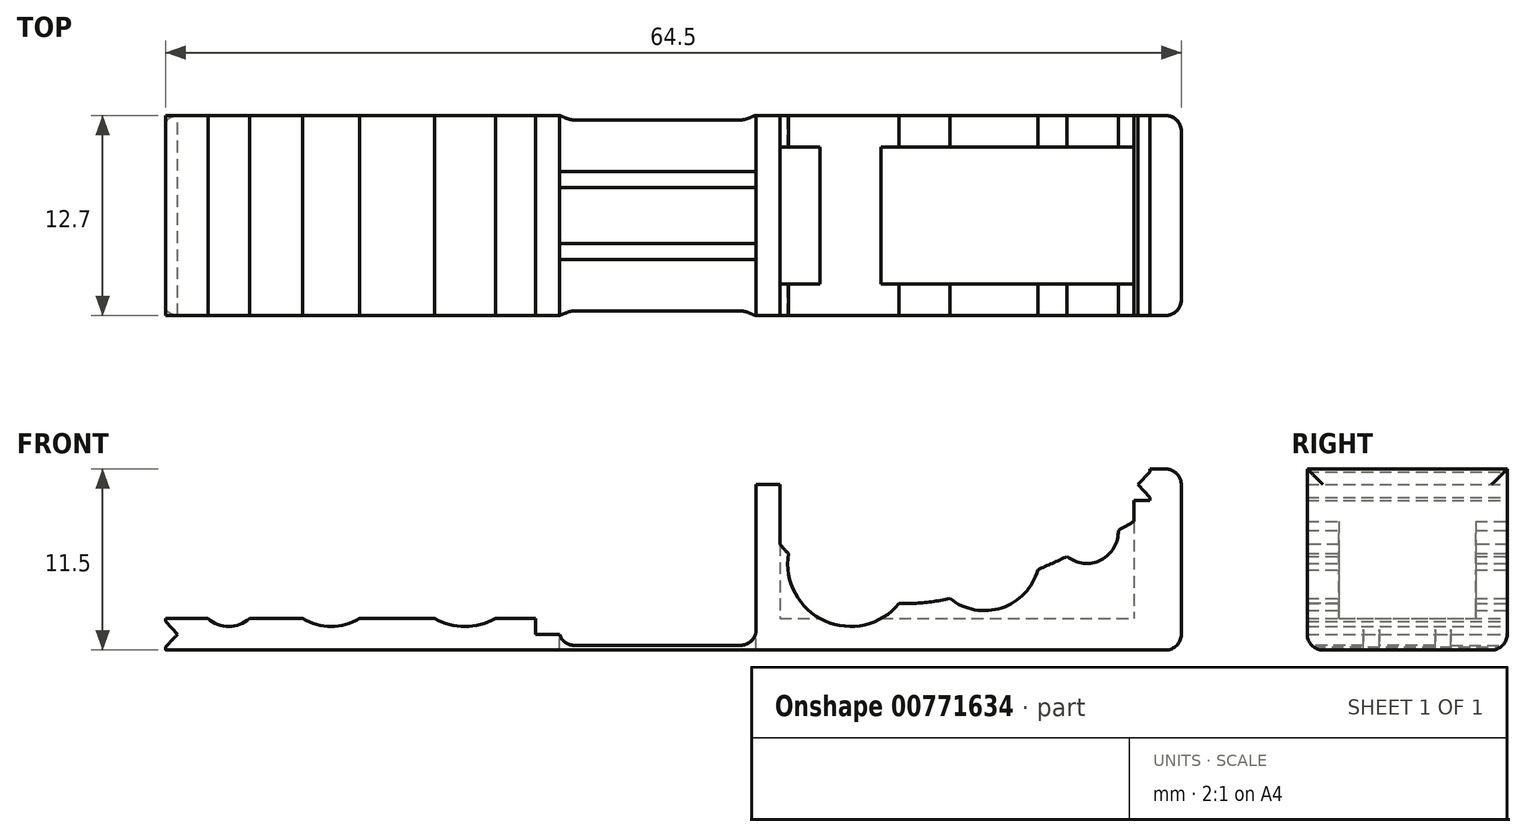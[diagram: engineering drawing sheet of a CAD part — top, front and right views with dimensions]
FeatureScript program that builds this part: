
annotation { "Feature Type Name" : "Feature", "Feature Type Description" : "" }
export const myFeature = defineFeature(function(context is Context, id is Id, definition is map)
    precondition{}
    {
        {
            var Q0;
            Q0=qCreatedBy(makeId("Front.planeOp"),FACE);
            var sketch = newSketch(context, id + "F0", { "sketchPlane" : qUnion([Q0])});
            skCircle(sketch, "E0", {"center": v(-12.25, 5.5) * mm, "radius": 4 * mm});
            skCircle(sketch, "E1", {"center": v(-20.75, 5) * mm, "radius": 3.5 * mm});
            skCircle(sketch, "E2", {"center": v(-27.25, 3.5) * mm, "radius": 2 * mm});
            skPoint(sketch, "E3", {"position": v(-20.75, 1.5) * mm});
            skPoint(sketch, "E4", {"position": v(-27.25, 1.5) * mm});
            skPoint(sketch, "E5", {"position": v(-12.25, 1.5) * mm});
            skLineSegment(sketch, "E6", {"start": v(-25.25, 1.5) * mm, "end": v(-24.25, 1.5) * mm});
            skLineSegment(sketch, "E7", {"start": v(-17.25, 1.5) * mm, "end": v(-16.25, 1.5) * mm});
            skPoint(sketch, "E8", {"position": v(-25.25, 3.5) * mm});
            skPoint(sketch, "E9", {"position": v(-24.25, 5) * mm});
            skPoint(sketch, "E10", {"position": v(-29.25, 3.5) * mm});
            skPoint(sketch, "E11", {"position": v(-17.25, 5) * mm});
            skPoint(sketch, "E12", {"position": v(-16.25, 5.5) * mm});
            skPoint(sketch, "E13", {"position": v(-8.25, 5.5) * mm});
            skPoint(sketch, "E14", {"position": v(0, 5.5) * mm});
            skPoint(sketch, "E15", {"position": v(12.25, 1.5) * mm});
            skCircle(sketch, "E16.1.0", {"center": v(12.25, 5.5) * mm, "radius": 4 * mm});
            skCircle(sketch, "E16.1.1", {"center": v(20.75, 6) * mm, "radius": 3.5 * mm});
            skCircle(sketch, "E16.1.2", {"center": v(27.25, 7.5) * mm, "radius": 2 * mm});
            skSolve(sketch);
        }
        {
            var Q0;
            Q0=qCreatedBy(makeId("Front.planeOp"),FACE);
            var sketch = newSketch(context, id + "F1", { "sketchPlane" : qUnion([Q0])});
            skCircle(sketch, "E17.0", {"center": v(-27.25, 3.5) * mm, "radius": 2 * mm});
            skCircle(sketch, "E18.0", {"center": v(-20.75, 5) * mm, "radius": 3.5 * mm});
            skCircle(sketch, "E19.0", {"center": v(-12.25, 5.5) * mm, "radius": 4 * mm});
            skLineSegment(sketch, "E20.bottom", {"start": v(-31.25, 2) * mm, "end": v(-6.25, 2) * mm});
            skLineSegment(sketch, "E20.top", {"start": v(-31.25, 0) * mm, "end": v(-6.25, 0) * mm});
            skLineSegment(sketch, "E20.left", {"start": v(-31.25, 2) * mm, "end": v(-31.25, 0) * mm});
            skLineSegment(sketch, "E20.right", {"start": v(-6.25, 2) * mm, "end": v(-6.25, 0) * mm});
            skLineSegment(sketch, "E21.bottom", {"start": v(6.25, 0) * mm, "end": v(31.25, 0) * mm});
            skLineSegment(sketch, "E21.left", {"start": v(6.25, 0) * mm, "end": v(6.25, 8.72) * mm});
            skLineSegment(sketch, "E21.right", {"start": v(31.25, 0) * mm, "end": v(31.25, 8.72) * mm});
            skLineSegment(sketch, "E22.bottom", {"start": v(-6.25, 0.3) * mm, "end": v(6.25, 0.3) * mm});
            skLineSegment(sketch, "E22.top", {"start": v(-6.25, 0) * mm, "end": v(6.25, 0) * mm});
            skLineSegment(sketch, "E22.left", {"start": v(-6.25, 0.3) * mm, "end": v(-6.25, 0) * mm});
            skLineSegment(sketch, "E22.right", {"start": v(6.25, 0.3) * mm, "end": v(6.25, 0) * mm});
            skPoint(sketch, "E23", {"position": v(0, 0) * mm});
            skFitSpline(sketch, "E24", {"points": [v(6.25, 8.72) * mm, v(31.25, 8.72) * mm], "startDerivative": vector(15.22, -23.1) * mm, "endDerivative": vector(40.47, 23.1) * mm});
            skCircle(sketch, "E25.0", {"center": v(12.25, 5.5) * mm, "radius": 4 * mm});
            skCircle(sketch, "E26.0", {"center": v(20.75, 6) * mm, "radius": 3.5 * mm});
            skCircle(sketch, "E27.0", {"center": v(27.25, 7.5) * mm, "radius": 2 * mm});
            skSolve(sketch);
        }
        {
            var Q0;
            Q0=makeQuery(id+"F1.imprint","IMPRINT",FACE,{"disambiguationData":[TD([[makeQuery(id+"F1.imprint","IMPRINT",EDGE,{"derivedFrom":sQuery(id+"F1.wireOp",EDGE,"E20.top")}),1.0]])]});
            var Q1;
            Q1=makeQuery(id+"F1.imprint","IMPRINT",FACE,{"disambiguationData":[TD([[makeQuery(id+"F1.imprint","IMPRINT",EDGE,{"derivedFrom":sQuery(id+"F1.wireOp",EDGE,"E22.bottom")}),-1.0]])]});
            var Q2;
            Q2=makeQuery(id+"F1.imprint","IMPRINT",FACE,{"disambiguationData":[TD([[makeQuery(id+"F1.imprint","IMPRINT",EDGE,{"derivedFrom":sQuery(id+"F1.wireOp",EDGE,"E21.bottom")}),1.0]])]});
            extrude(context, id + "F2", {"entities" : qUnion([Q0, Q1, Q2]), "depth" : 12.7 * mm, "offsetDistance" : 25 * mm});
        }
        {
            var Q0;
            Q0=makeQuery(id+"F2.opExtrude","SWEPT_FACE",FACE,{"disambiguationData":[OSD([sQuery(id+"F1.wireOp",EDGE,"E21.right")])]});
            var sketch = newSketch(context, id + "F3", { "sketchPlane" : qUnion([Q0])});
            skLineSegment(sketch, "E28.bottom", {"start": v(-10.7, 8.72) * mm, "end": v(-2, 8.72) * mm});
            skLineSegment(sketch, "E28.top", {"start": v(-10.7, 2) * mm, "end": v(-2, 2) * mm});
            skLineSegment(sketch, "E28.left", {"start": v(-10.7, 8.72) * mm, "end": v(-10.7, 2) * mm});
            skLineSegment(sketch, "E28.right", {"start": v(-2, 8.72) * mm, "end": v(-2, 2) * mm});
            skPoint(sketch, "E29", {"position": v(-6.35, 8.72) * mm});
            skSolve(sketch);
        }
        {
            var Q0;
            Q0=qCreatedBy(makeId("Front.planeOp"),FACE);
            var sketch = newSketch(context, id + "F4", { "sketchPlane" : qUnion([Q0])});
            skLineSegment(sketch, "E30.0", {"start": v(-31.25, 2) * mm, "end": v(-31.25, 0) * mm});
            skLineSegment(sketch, "E31", {"start": v(-30.5, 1) * mm, "end": v(-31.25, 0.2) * mm});
            skLineSegment(sketch, "E32", {"start": v(31.25, 0) * mm, "end": v(33.25, 0) * mm});
            skLineSegment(sketch, "E33", {"start": v(33.25, 0) * mm, "end": v(33.25, 11.5) * mm});
            skLineSegment(sketch, "E34", {"start": v(33.25, 11.5) * mm, "end": v(31.25, 11.5) * mm});
            skLineSegment(sketch, "E35", {"start": v(31.25, 11.5) * mm, "end": v(31.25, 11.3) * mm});
            skLineSegment(sketch, "E36", {"start": v(31.25, 11.3) * mm, "end": v(30.5, 10.5) * mm});
            skLineSegment(sketch, "E37", {"start": v(30.5, 10.5) * mm, "end": v(31.25, 9.7) * mm});
            skLineSegment(sketch, "E38", {"start": v(31.25, 9.7) * mm, "end": v(31.25, 9.5) * mm});
            skLineSegment(sketch, "E39", {"start": v(31.25, 9.5) * mm, "end": v(30.25, 9.5) * mm});
            skLineSegment(sketch, "E40", {"start": v(30.25, 9.5) * mm, "end": v(30.25, 0) * mm});
            skPoint(sketch, "E41.0", {"position": v(-6.25, 2) * mm});
            skLineSegment(sketch, "E42.bottom", {"start": v(-6.25, 2) * mm, "end": v(-7.75, 2) * mm});
            skLineSegment(sketch, "E42.top", {"start": v(-6.25, 1) * mm, "end": v(-7.75, 1) * mm});
            skLineSegment(sketch, "E42.left", {"start": v(-6.25, 2) * mm, "end": v(-6.25, 1) * mm});
            skLineSegment(sketch, "E42.right", {"start": v(-7.75, 2) * mm, "end": v(-7.75, 1) * mm});
            skLineSegment(sketch, "E43", {"start": v(6.25, 0) * mm, "end": v(6.25, 11.5) * mm});
            skLineSegment(sketch, "E44", {"start": v(6.25, 11.5) * mm, "end": v(7.75, 11.5) * mm});
            skLineSegment(sketch, "E45", {"start": v(7.75, 11.5) * mm, "end": v(7.75, 0) * mm});
            skLineSegment(sketch, "E46", {"start": v(7.75, 10.5) * mm, "end": v(6.25, 10.5) * mm});
            skLineSegment(sketch, "E47", {"start": v(-31.25, 0.2) * mm, "end": v(-31.25, 0) * mm});
            skLineSegment(sketch, "E48", {"start": v(-30.5, 1) * mm, "end": v(-31.25, 1.8) * mm});
            skLineSegment(sketch, "E49", {"start": v(-30.5, 1) * mm, "end": v(-31.25, 1) * mm});
            skLineSegment(sketch, "E50", {"start": v(31.25, 11.3) * mm, "end": v(31.25, 9.7) * mm});
            skLineSegment(sketch, "E51", {"start": v(30.5, 10.5) * mm, "end": v(31.25, 10.5) * mm});
            skLineSegment(sketch, "E52", {"start": v(6.25, 0) * mm, "end": v(7.75, 0) * mm});
            skLineSegment(sketch, "E53", {"start": v(31.25, 0) * mm, "end": v(30.25, 0) * mm});
            skSolve(sketch);
        }
        {
            var Q0;
            Q0=makeQuery(id+"F3.imprint","IMPRINT",FACE,{"disambiguationData":[TD([[makeQuery(id+"F3.imprint","IMPRINT",EDGE,{"derivedFrom":sQuery(id+"F3.wireOp",EDGE,"E28.bottom")}),-1.0]])]});
            var Q1;
            Q1=sQuery(id+"F4.wireOp",VERTEX,"E44.end");
            var Q2;
            Q2=sQuery(id+"F4.wireOp",VERTEX,"E39.end");
            extrude(context, id + "F5", {"entities" : qUnion([Q0]), "operationType" : NewBodyOperationType.REMOVE, "endBound" : BoundingType.UP_TO_VERTEX, "oppositeDirection" : true, "depth" : 25 * mm, "endBoundEntityVertex" : qUnion([Q1]), "offsetDistance" : 25 * mm, "hasSecondDirection" : true, "secondDirectionBound" : SecondDirectionBoundingType.UP_TO_VERTEX, "secondDirectionOppositeDirection" : true, "secondDirectionDepth" : 1 * mm, "secondDirectionBoundEntityVertex" : qUnion([Q2])});
        }
        {
            var Q0;
            Q0=makeQuery(id+"F4.imprint","IMPRINT",FACE,{"disambiguationData":[TD([[makeQuery(id+"F4.imprint","IMPRINT",EDGE,{"derivedFrom":sQuery(id+"F4.wireOp",EDGE,"E42.bottom")}),1.0]])]});
            var Q1;
            {var subQ0=sQuery(id+"F4.wireOp",EDGE,"E48");Q1=makeQuery(id+"F4.imprint","IMPRINT",FACE,{"disambiguationData":[TD([[makeQuery(id+"F4.imprint","IMPRINT",EDGE,{"derivedFrom":subQ0}),1.0]])]});}
            var Q2;
            {var subQ0=sQuery(id+"F4.wireOp",EDGE,"E31");Q2=makeQuery(id+"F4.imprint","IMPRINT",FACE,{"disambiguationData":[TD([[makeQuery(id+"F4.imprint","IMPRINT",EDGE,{"derivedFrom":subQ0}),-1.0]])]});}
            var Q3;
            Q3=makeQuery(id+"F2.opExtrude","CAP_FACE",FACE,{"disambiguationData":[OSD([sQuery(id+"F1.wireOp",EDGE,"E17.0"),sQuery(id+"F1.wireOp",EDGE,"E18.0"),sQuery(id+"F1.wireOp",EDGE,"E19.0"),sQuery(id+"F1.wireOp",EDGE,"39558c70-f25f-4615-a4fc-9f10651319aa.0"),sQuery(id+"F1.wireOp",EDGE,"80cb3f8d-76fc-4d8c-9657-01cc7cf24295.0"),sQuery(id+"F1.wireOp",EDGE,"e33433a3-29e9-4e5c-a5f5-65428797577c.0"),sQuery(id+"F1.wireOp",EDGE,"f559ebbb-155e-4eeb-81d7-9a44377361a2.0"),sQuery(id+"F1.wireOp",EDGE,"83c2658b-0a7b-448c-8bf9-07c5c6f78f0d.0"),sQuery(id+"F1.wireOp",EDGE,"bfc84c2d-0466-46b3-b6ee-57e5656d9882.0"),sQuery(id+"F1.wireOp",EDGE,"843dab0d-1d24-4ee7-8fdb-ab5b204e5594.0"),sQuery(id+"F1.wireOp",EDGE,"b1db5fe8-4577-4f43-9009-2c0ead2f0b42.0"),sQuery(id+"F1.wireOp",EDGE,"7c9d848a-de27-417e-884b-11b5ffe38909.0"),sQuery(id+"F1.wireOp",EDGE,"E20.bottom"),sQuery(id+"F1.wireOp",EDGE,"E20.top"),sQuery(id+"F1.wireOp",EDGE,"E20.left"),sQuery(id+"F1.wireOp",EDGE,"E20.right"),sQuery(id+"F1.wireOp",EDGE,"E21.bottom"),sQuery(id+"F1.wireOp",EDGE,"E21.left"),sQuery(id+"F1.wireOp",EDGE,"E21.right"),sQuery(id+"F1.wireOp",EDGE,"E22.bottom"),sQuery(id+"F1.wireOp",EDGE,"E22.top"),sQuery(id+"F1.wireOp",EDGE,"E24")])],"isStart":false});
            extrude(context, id + "F6", {"entities" : qUnion([Q0, Q1, Q2]), "operationType" : NewBodyOperationType.REMOVE, "endBound" : BoundingType.UP_TO_SURFACE, "depth" : 25 * mm, "endBoundEntityFace" : qUnion([Q3]), "offsetDistance" : 25 * mm});
        }
        {
            var Q0;
            Q0=makeQuery(id+"F4.imprint","IMPRINT",FACE,{"disambiguationData":[TD([[makeQuery(id+"F4.imprint","IMPRINT",EDGE,{"derivedFrom":sQuery(id+"F4.wireOp",EDGE,"E32")}),1.0]])]});
            var Q1;
            {var subQ2=sQuery(id+"F4.wireOp",EDGE,"E46");Q1=makeQuery(id+"F4.imprint","IMPRINT",FACE,{"disambiguationData":[TD([[makeQuery(id+"F4.imprint","IMPRINT",EDGE,{"derivedFrom":subQ2}),1.0]])]});}
            var Q2;
            {var subQ0=sQuery(id+"F4.wireOp",EDGE,"E37");Q2=makeQuery(id+"F4.imprint","IMPRINT",FACE,{"disambiguationData":[TD([[makeQuery(id+"F4.imprint","IMPRINT",EDGE,{"derivedFrom":subQ0}),1.0]])]});}
            var Q3;
            {var subQ0=sQuery(id+"F4.wireOp",EDGE,"E36");Q3=makeQuery(id+"F4.imprint","IMPRINT",FACE,{"disambiguationData":[TD([[makeQuery(id+"F4.imprint","IMPRINT",EDGE,{"derivedFrom":subQ0}),1.0]])]});}
            var Q4;
            Q4=makeQuery(id+"F2.opExtrude","CAP_FACE",FACE,{"disambiguationData":[OSD([sQuery(id+"F1.wireOp",EDGE,"E17.0"),sQuery(id+"F1.wireOp",EDGE,"E18.0"),sQuery(id+"F1.wireOp",EDGE,"E19.0"),sQuery(id+"F1.wireOp",EDGE,"39558c70-f25f-4615-a4fc-9f10651319aa.0"),sQuery(id+"F1.wireOp",EDGE,"80cb3f8d-76fc-4d8c-9657-01cc7cf24295.0"),sQuery(id+"F1.wireOp",EDGE,"e33433a3-29e9-4e5c-a5f5-65428797577c.0"),sQuery(id+"F1.wireOp",EDGE,"f559ebbb-155e-4eeb-81d7-9a44377361a2.0"),sQuery(id+"F1.wireOp",EDGE,"83c2658b-0a7b-448c-8bf9-07c5c6f78f0d.0"),sQuery(id+"F1.wireOp",EDGE,"bfc84c2d-0466-46b3-b6ee-57e5656d9882.0"),sQuery(id+"F1.wireOp",EDGE,"843dab0d-1d24-4ee7-8fdb-ab5b204e5594.0"),sQuery(id+"F1.wireOp",EDGE,"b1db5fe8-4577-4f43-9009-2c0ead2f0b42.0"),sQuery(id+"F1.wireOp",EDGE,"7c9d848a-de27-417e-884b-11b5ffe38909.0"),sQuery(id+"F1.wireOp",EDGE,"E20.bottom"),sQuery(id+"F1.wireOp",EDGE,"E20.top"),sQuery(id+"F1.wireOp",EDGE,"E20.left"),sQuery(id+"F1.wireOp",EDGE,"E20.right"),sQuery(id+"F1.wireOp",EDGE,"E21.bottom"),sQuery(id+"F1.wireOp",EDGE,"E21.left"),sQuery(id+"F1.wireOp",EDGE,"E21.right"),sQuery(id+"F1.wireOp",EDGE,"E22.bottom"),sQuery(id+"F1.wireOp",EDGE,"E22.top"),sQuery(id+"F1.wireOp",EDGE,"E24")])],"isStart":false});
            extrude(context, id + "F7", {"entities" : qUnion([Q0, Q1, Q2, Q3]), "operationType" : NewBodyOperationType.ADD, "endBound" : BoundingType.UP_TO_SURFACE, "depth" : 25 * mm, "endBoundEntityFace" : qUnion([Q4]), "offsetDistance" : 25 * mm});
        }
        {
            var Q0;
            Q0=makeQuery(id+"F2.opExtrude","SWEPT_FACE",FACE,{"disambiguationData":[OSD([sQuery(id+"F1.wireOp",EDGE,"E22.bottom")])]});
            var sketch = newSketch(context, id + "F8", { "sketchPlane" : qUnion([Q0])});
            skLineSegment(sketch, "E54.bottom", {"start": v(6.25, -12.7) * mm, "end": v(-6.25, -12.7) * mm});
            skLineSegment(sketch, "E54.top", {"start": v(6.25, -9.13) * mm, "end": v(-6.25, -9.13) * mm});
            skLineSegment(sketch, "E54.left", {"start": v(6.25, -12.7) * mm, "end": v(6.25, -9.13) * mm});
            skLineSegment(sketch, "E54.right", {"start": v(-6.25, -12.7) * mm, "end": v(-6.25, -9.13) * mm});
            skLineSegment(sketch, "E55.bottom", {"start": v(6.25, -8.13) * mm, "end": v(-6.25, -8.13) * mm});
            skLineSegment(sketch, "E55.top", {"start": v(6.25, -4.57) * mm, "end": v(-6.25, -4.57) * mm});
            skLineSegment(sketch, "E55.left", {"start": v(6.25, -8.13) * mm, "end": v(6.25, -4.57) * mm});
            skLineSegment(sketch, "E55.right", {"start": v(-6.25, -8.13) * mm, "end": v(-6.25, -4.57) * mm});
            skLineSegment(sketch, "E56.bottom", {"start": v(6.25, -3.57) * mm, "end": v(-6.25, -3.57) * mm});
            skLineSegment(sketch, "E56.top", {"start": v(6.25, 0) * mm, "end": v(-6.25, 0) * mm});
            skLineSegment(sketch, "E56.left", {"start": v(6.25, -3.57) * mm, "end": v(6.25, 0) * mm});
            skLineSegment(sketch, "E56.right", {"start": v(-6.25, -3.57) * mm, "end": v(-6.25, 0) * mm});
            skLineSegment(sketch, "E57", {"start": v(6.25, -9.13) * mm, "end": v(6.25, -8.13) * mm});
            skLineSegment(sketch, "E58", {"start": v(6.25, -4.57) * mm, "end": v(6.25, -3.57) * mm});
            skSolve(sketch);
        }
        {
            var Q0;
            {var subQ0=sQuery(id+"F8.wireOp",EDGE,"E54.top");Q0=makeQuery(id+"F8.imprint","IMPRINT",FACE,{"disambiguationData":[TD([[makeQuery(id+"F8.imprint","IMPRINT",EDGE,{"derivedFrom":subQ0}),-1.0]])]});}
            var Q1;
            {var subQ0=sQuery(id+"F8.wireOp",EDGE,"E55.top");Q1=makeQuery(id+"F8.imprint","IMPRINT",FACE,{"disambiguationData":[TD([[makeQuery(id+"F8.imprint","IMPRINT",EDGE,{"derivedFrom":subQ0}),-1.0]])]});}
            var Q2;
            Q2=makeQuery(id+"F2.opExtrude","SWEPT_FACE",FACE,{"disambiguationData":[OSD([sQuery(id+"F1.wireOp",EDGE,"E20.top"),sQuery(id+"F1.wireOp",EDGE,"E21.bottom"),sQuery(id+"F1.wireOp",EDGE,"E22.top")])]});
            extrude(context, id + "F9", {"entities" : qUnion([Q0, Q1]), "operationType" : NewBodyOperationType.REMOVE, "endBound" : BoundingType.UP_TO_SURFACE, "oppositeDirection" : true, "depth" : 25 * mm, "endBoundEntityFace" : qUnion([Q2]), "offsetDistance" : 25 * mm});
        }
        {
            var Q0;
            {var subQ0=sQuery(id+"F1.wireOp",EDGE,"E22.bottom");var subQ1=sQuery(id+"F1.wireOp",EDGE,"E21.left");Q0=makeQuery(id+"F9.boolean.opBoolean","SPLIT",EDGE,{"disambiguationData":[TD([makeQuery(id+"F9.opExtrude","SWEPT_FACE",FACE,{"disambiguationData":[OSD([sQuery(id+"F8.wireOp",EDGE,"E54.top")])]})])],"derivedFrom":makeQuery(id+"F2.opExtrude","SWEPT_EDGE",EDGE,{"disambiguationData":[OSD([subQ1,subQ0,sQuery(id+"F1.wireOp",EDGE,"E22.right")])]})});}
            var Q1;
            {var subQ0=sQuery(id+"F1.wireOp",EDGE,"E22.bottom");var subQ1=sQuery(id+"F1.wireOp",EDGE,"E21.left");Q1=makeQuery(id+"F9.boolean.opBoolean","SPLIT",EDGE,{"disambiguationData":[TD([makeQuery(id+"F9.opExtrude","SWEPT_FACE",FACE,{"disambiguationData":[OSD([sQuery(id+"F8.wireOp",EDGE,"E55.bottom")])]})])],"derivedFrom":makeQuery(id+"F2.opExtrude","SWEPT_EDGE",EDGE,{"disambiguationData":[OSD([subQ1,subQ0,sQuery(id+"F1.wireOp",EDGE,"E22.right")])]})});}
            var Q2;
            {var subQ1=sQuery(id+"F1.wireOp",EDGE,"E22.bottom");var subQ2=sQuery(id+"F1.wireOp",EDGE,"E21.left");Q2=makeQuery(id+"F9.boolean.opBoolean","SPLIT",EDGE,{"disambiguationData":[TD([makeQuery(id+"F9.opExtrude","SWEPT_FACE",FACE,{"disambiguationData":[OSD([sQuery(id+"F8.wireOp",EDGE,"E56.bottom")])]})])],"derivedFrom":makeQuery(id+"F2.opExtrude","SWEPT_EDGE",EDGE,{"disambiguationData":[OSD([subQ2,subQ1,sQuery(id+"F1.wireOp",EDGE,"E22.right")])]})});}
            var Q3;
            {var subQ0=sQuery(id+"F1.wireOp",EDGE,"E22.bottom");var subQ1=sQuery(id+"F1.wireOp",EDGE,"E20.right");var subQ2=sQuery(id+"F1.wireOp",EDGE,"E22.left");var subQ3=makeQuery(id+"F2.opExtrude","SWEPT_EDGE",EDGE,{"disambiguationData":[OSD([subQ1,subQ0,subQ2])]});var subQ5=sQuery(id+"F8.wireOp",EDGE,"E56.bottom");Q3=makeQuery(id+"F9.boolean.opBoolean","SPLIT",EDGE,{"disambiguationData":[TD([makeQuery(id+"F9.opExtrude","SWEPT_FACE",FACE,{"disambiguationData":[OSD([subQ5])]})])],"derivedFrom":subQ3});}
            var Q4;
            {var subQ0=sQuery(id+"F8.wireOp",EDGE,"E55.bottom");var subQ1=sQuery(id+"F1.wireOp",EDGE,"E22.bottom");var subQ3=sQuery(id+"F1.wireOp",EDGE,"E20.right");var subQ4=sQuery(id+"F1.wireOp",EDGE,"E22.left");var subQ5=makeQuery(id+"F2.opExtrude","SWEPT_EDGE",EDGE,{"disambiguationData":[OSD([subQ3,subQ1,subQ4])]});Q4=makeQuery(id+"F9.boolean.opBoolean","SPLIT",EDGE,{"disambiguationData":[TD([makeQuery(id+"F9.opExtrude","SWEPT_FACE",FACE,{"disambiguationData":[OSD([subQ0])]})])],"derivedFrom":subQ5});}
            var Q5;
            {var subQ0=sQuery(id+"F1.wireOp",EDGE,"E22.bottom");var subQ1=sQuery(id+"F1.wireOp",EDGE,"E20.right");var subQ2=sQuery(id+"F8.wireOp",EDGE,"E54.top");var subQ4=sQuery(id+"F1.wireOp",EDGE,"E22.left");var subQ5=makeQuery(id+"F2.opExtrude","SWEPT_EDGE",EDGE,{"disambiguationData":[OSD([subQ1,subQ0,subQ4])]});Q5=makeQuery(id+"F9.boolean.opBoolean","SPLIT",EDGE,{"disambiguationData":[TD([makeQuery(id+"F9.opExtrude","SWEPT_FACE",FACE,{"disambiguationData":[OSD([subQ2])]})])],"derivedFrom":subQ5});}
            fillet(context, id + "F10", {"entities" : qUnion([Q0, Q1, Q2, Q3, Q4, Q5]), "radius" : 1 * mm, "tangentPropagation" : true, "allowEdgeOverflow" : false});
        }
        {
            var Q0;
            Q0=makeQuery(id+"F7.boolean.opBoolean","MERGE",EDGE,{"derivedFrom":[makeQuery(id+"F2.opExtrude","CAP_EDGE",EDGE,{"disambiguationData":[OSD([sQuery(id+"F1.wireOp",EDGE,"E20.top"),sQuery(id+"F1.wireOp",EDGE,"E21.bottom"),sQuery(id+"F1.wireOp",EDGE,"E22.top")])],"isStart":true}),makeQuery(id+"F7.opExtrude","CAP_EDGE",EDGE,{"disambiguationData":[OSD([sQuery(id+"F4.wireOp",EDGE,"E32"),sQuery(id+"F4.wireOp",EDGE,"E53")])],"isStart":true})]});
            var Q1;
            Q1=makeQuery(id+"F7.boolean.opBoolean","MERGE",EDGE,{"derivedFrom":[makeQuery(id+"F2.opExtrude","CAP_EDGE",EDGE,{"disambiguationData":[OSD([sQuery(id+"F1.wireOp",EDGE,"E20.top"),sQuery(id+"F1.wireOp",EDGE,"E21.bottom"),sQuery(id+"F1.wireOp",EDGE,"E22.top")])],"isStart":false}),makeQuery(id+"F7.opExtrude","CAP_EDGE",EDGE,{"disambiguationData":[OSD([sQuery(id+"F4.wireOp",EDGE,"E32"),sQuery(id+"F4.wireOp",EDGE,"E53")])],"isStart":false})]});
            var Q2;
            Q2=makeQuery(id+"F7.opExtrude","SWEPT_EDGE",EDGE,{"disambiguationData":[OSD([sQuery(id+"F4.wireOp",EDGE,"E32"),sQuery(id+"F4.wireOp",EDGE,"E33")])]});
            var Q3;
            {var subQ0=sQuery(id+"F1.wireOp",EDGE,"E20.left");Q3=makeQuery(id+"F6.boolean.opBoolean","SPLIT",EDGE,{"disambiguationData":[TD([makeQuery(id+"F6.opExtrude","SWEPT_FACE",FACE,{"disambiguationData":[OSD([sQuery(id+"F4.wireOp",EDGE,"Ho0J7W4c-XaMj-GwMl-eiW3-HM9fCfqAVLBn")])]})])],"derivedFrom":makeQuery(id+"F2.opExtrude","CAP_EDGE",EDGE,{"disambiguationData":[OSD([subQ0])],"isStart":true})});}
            var Q4;
            {var subQ0=sQuery(id+"F1.wireOp",EDGE,"E20.left");Q4=makeQuery(id+"F6.boolean.opBoolean","SPLIT",EDGE,{"disambiguationData":[TD([makeQuery(id+"F6.opExtrude","SWEPT_FACE",FACE,{"disambiguationData":[OSD([sQuery(id+"F4.wireOp",EDGE,"Ho0J7W4c-XaMj-GwMl-eiW3-HM9fCfqAVLBn")])]})])],"derivedFrom":makeQuery(id+"F2.opExtrude","CAP_EDGE",EDGE,{"disambiguationData":[OSD([subQ0])],"isStart":false})});}
            var Q5;
            Q5=makeQuery(id+"F7.opExtrude","CAP_EDGE",EDGE,{"disambiguationData":[OSD([sQuery(id+"F4.wireOp",EDGE,"E33")])],"isStart":false});
            var Q6;
            Q6=makeQuery(id+"F7.opExtrude","CAP_EDGE",EDGE,{"disambiguationData":[OSD([sQuery(id+"F4.wireOp",EDGE,"E33")])],"isStart":true});
            var Q7;
            Q7=makeQuery(id+"F7.opExtrude","SWEPT_EDGE",EDGE,{"disambiguationData":[OSD([sQuery(id+"F4.wireOp",EDGE,"E33"),sQuery(id+"F4.wireOp",EDGE,"E34")])]});
            fillet(context, id + "F11", {"entities" : qUnion([Q0, Q1, Q2, Q3, Q4, Q5, Q6, Q7]), "radius" : 1 * mm, "tangentPropagation" : true, "allowEdgeOverflow" : false});
        }
    });
